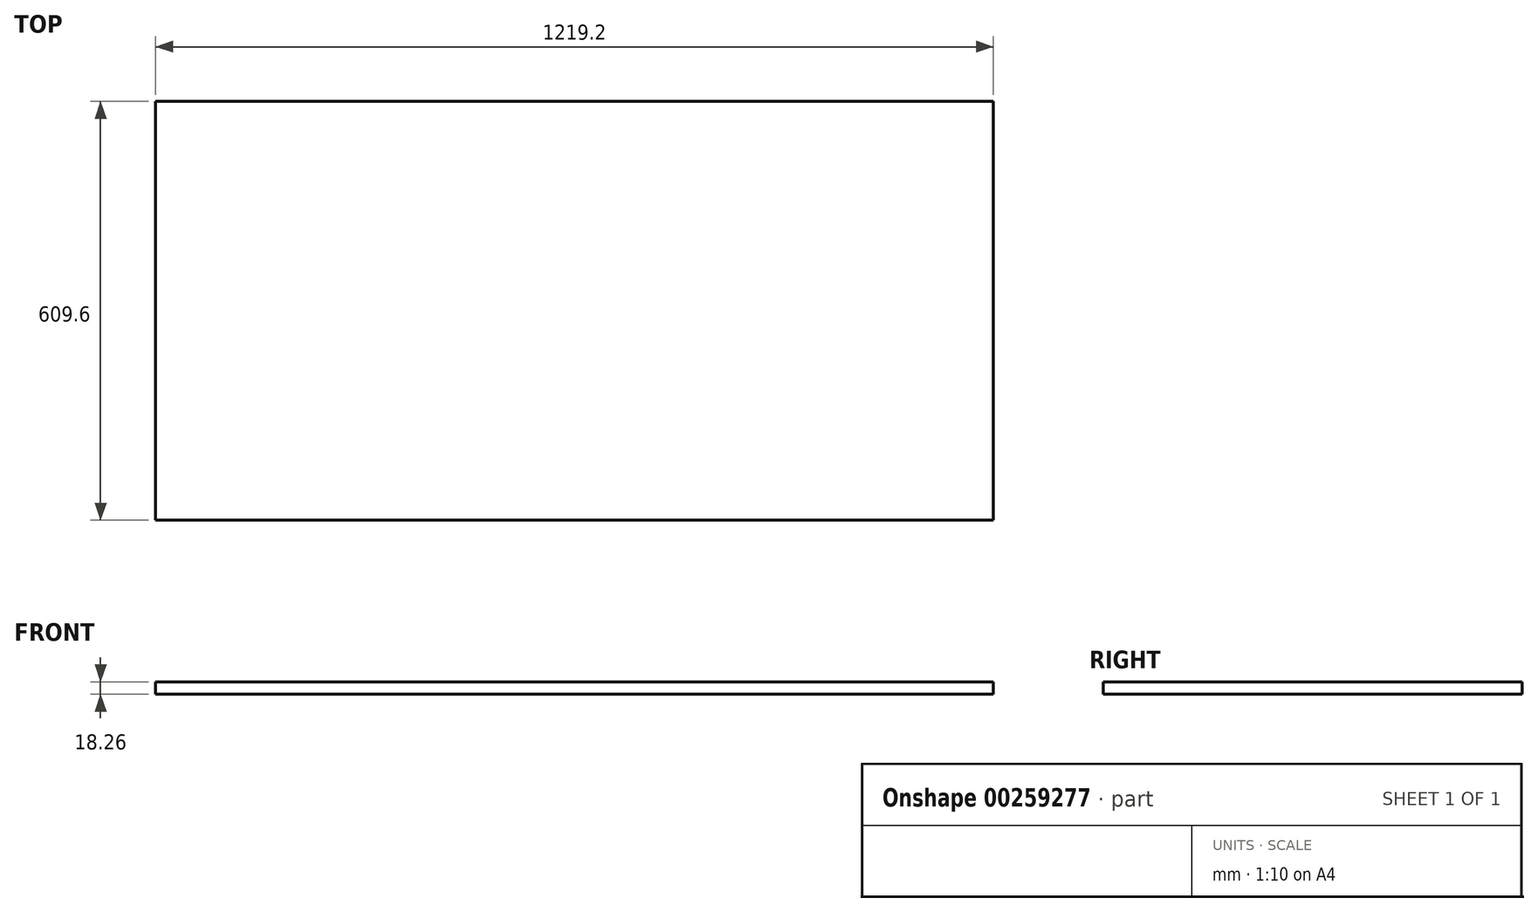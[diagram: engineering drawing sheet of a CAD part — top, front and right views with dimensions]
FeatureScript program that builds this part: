
annotation { "Feature Type Name" : "Feature", "Feature Type Description" : "" }
export const myFeature = defineFeature(function(context is Context, id is Id, definition is map)
    precondition{}
    {
        {
            var Q0;
            Q0=qCreatedBy(makeId("Top.planeOp"),FACE);
            var sketch = newSketch(context, id + "F0", { "sketchPlane" : qUnion([Q0])});
            skLineSegment(sketch, "E0.bottom", {"start": v(-609.6, 304.8) * mm, "end": v(609.6, 304.8) * mm});
            skLineSegment(sketch, "E0.top", {"start": v(-609.6, -304.8) * mm, "end": v(609.6, -304.8) * mm});
            skLineSegment(sketch, "E0.left", {"start": v(-609.6, 304.8) * mm, "end": v(-609.6, -304.8) * mm});
            skLineSegment(sketch, "E0.right", {"start": v(609.6, 304.8) * mm, "end": v(609.6, -304.8) * mm});
            skPoint(sketch, "E0.middle", {"position": v(0, 0) * mm});
            skSolve(sketch);
        }
        {
            var Q0;
            Q0=makeQuery(id+"F0.imprint","IMPRINT",FACE,{"disambiguationData":[TD([[makeQuery(id+"F0.imprint","IMPRINT",EDGE,{"derivedFrom":sQuery(id+"F0.wireOp",EDGE,"E0.bottom")}),-1.0]])]});
            extrude(context, id + "F1", {"entities" : qUnion([Q0]), "depth" : 18.26 * mm});
        }
    });
